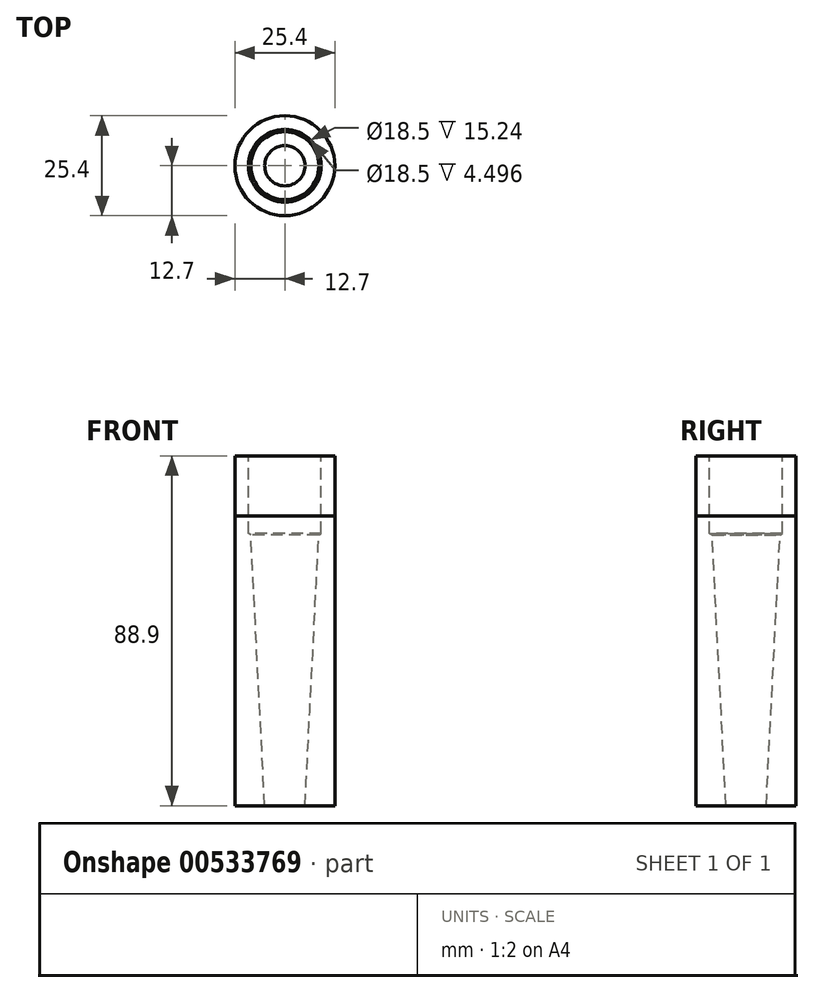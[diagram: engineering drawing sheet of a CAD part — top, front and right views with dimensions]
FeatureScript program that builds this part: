
annotation { "Feature Type Name" : "Feature", "Feature Type Description" : "" }
export const myFeature = defineFeature(function(context is Context, id is Id, definition is map)
    precondition{}
    {
        {
            var Q0;
            Q0=qCreatedBy(makeId("Top.planeOp"),FACE);
            var sketch = newSketch(context, id + "F0", { "sketchPlane" : qUnion([Q0])});
            skCircle(sketch, "E0", {"center": v(0, 0) * mm, "radius": 12.7 * mm});
            skSolve(sketch);
        }
        {
            var Q0;
            Q0=makeQuery(id+"F0.imprint","IMPRINT",FACE,{"disambiguationData":[TD([[makeQuery(id+"F0.imprint","IMPRINT",EDGE,{"derivedFrom":sQuery(id+"F0.wireOp",EDGE,"E0")}),1.0]])]});
            extrude(context, id + "F1", {"entities" : qUnion([Q0]), "depth" : 73.66 * mm, "offsetDistance" : 25.4 * mm, "hasDraft" : true, "draftAngle" : 0 * degree});
        }
        {
            var Q0;
            Q0=qCreatedBy(makeId("Top.planeOp"),FACE);
            var sketch = newSketch(context, id + "F2", { "sketchPlane" : qUnion([Q0])});
            skCircle(sketch, "E1", {"center": v(0, 0) * mm, "radius": 5.11 * mm});
            skSolve(sketch);
        }
        {
            var Q0;
            Q0=makeQuery(id+"F2.imprint","IMPRINT",FACE,{"disambiguationData":[TD([[makeQuery(id+"F2.imprint","IMPRINT",EDGE,{"derivedFrom":sQuery(id+"F2.wireOp",EDGE,"E1")}),1.0]])]});
            extrude(context, id + "F3", {"entities" : qUnion([Q0]), "operationType" : NewBodyOperationType.REMOVE, "endBound" : BoundingType.THROUGH_ALL, "depth" : 25.4 * mm, "offsetDistance" : 25.4 * mm, "hasDraft" : true, "draftAngle" : 2.94 * degree});
        }
        {
            var Q0;
            Q0=makeQuery(id+"F1.opExtrude","CAP_FACE",FACE,{"disambiguationData":[OSD([sQuery(id+"F0.wireOp",EDGE,"E0")])],"isStart":false});
            var sketch = newSketch(context, id + "F4", { "sketchPlane" : qUnion([Q0])});
            skCircle(sketch, "E2", {"center": v(0, 0) * mm, "radius": 12.7 * mm});
            skSolve(sketch);
        }
        {
            var Q0;
            Q0 = qSketchRegion(id + "F4", true);
            extrude(context, id + "F5", {"entities" : qUnion([Q0]), "depth" : 15.24 * mm, "offsetDistance" : 25.4 * mm});
        }
        {
            var Q0;
            Q0=makeQuery(id+"F5.opExtrude","CAP_FACE",FACE,{"disambiguationData":[OSD([sQuery(id+"F4.wireOp",EDGE,"E2")])],"isStart":false});
            cPlane(context, id + "F6", {"entities" : qUnion([Q0]), "cplaneType" : CPlaneType.OFFSET, "offset" : 0 * mm, "width" : 152.4 * mm, "height" : 152.4 * mm});
        }
        {
            var Q0;
            Q0=qCreatedBy(id+"F6.planeOp",FACE);
            var sketch = newSketch(context, id + "F7", { "sketchPlane" : qUnion([Q0])});
            skPoint(sketch, "E3", {"position": v(0, 0) * mm});
            skSolve(sketch);
        }
        {
            var Q0;
            Q0=sQuery(id+"F7.wireOp",VERTEX,"E3");
            var Q1;
            Q1=makeQuery(id+"F1.opExtrude","SWEPT_BODY",BODY,{"disambiguationData":[OSD([sQuery(id+"F0.wireOp",EDGE,"E0")])]});
            var Q2;
            Q2=makeQuery(id+"F5.opExtrude","SWEPT_BODY",BODY,{"disambiguationData":[OSD([sQuery(id+"F4.wireOp",EDGE,"E2")])]});
            hole(context, id + "F8", {"style" : HoleStyle.SIMPLE, "endStyle" : HoleEndStyle.BLIND, "standardTappedOrClearance" : lookupTablePath({ "standard" : "ISO", "engagement" : "75%", "pitch" : "1.5 mm", "size" : "M20", "type" : "Tapped" }), "standardBlindInLast" : lookupTablePath({ "standard" : "ISO", "engagement" : "75%", "pitch" : "1.5 mm", "size" : "M20", "type" : "Tapped" }), "holeDiameter" : 18.5 * mm, "showTappedDepth" : true, "holeDepth" : 19.74 * mm, "isTappedThrough" : true, "tappedDepth" : 15.24 * mm, "tapClearance" : 3, "startFromSketch" : true, "locations" : qUnion([Q0]), "scope" : qUnion([Q1, Q2]), "majorDiameter" : 20 * mm});
        }
    });
